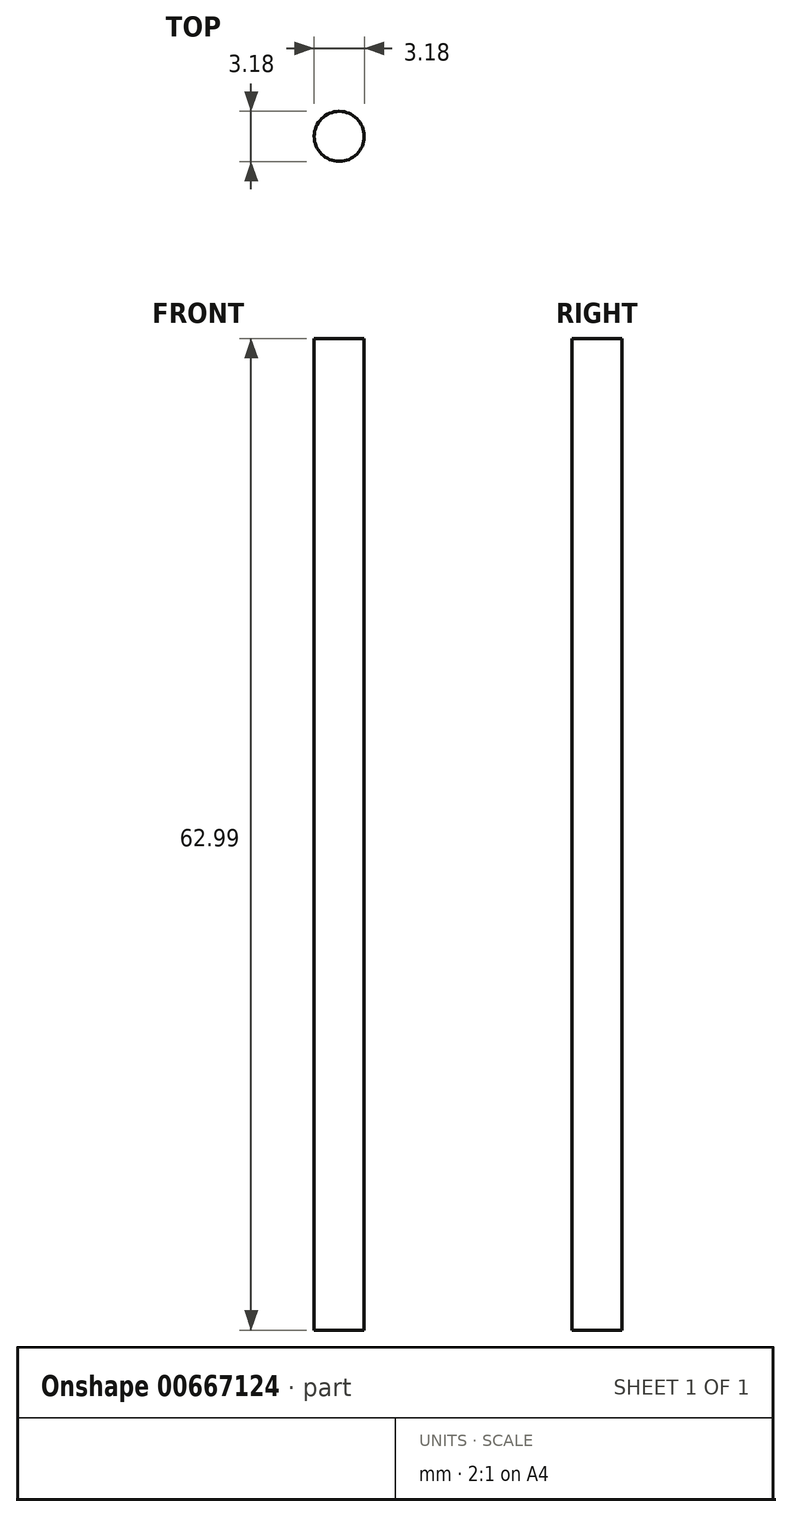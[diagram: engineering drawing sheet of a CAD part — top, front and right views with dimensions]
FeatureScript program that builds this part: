
annotation { "Feature Type Name" : "Feature", "Feature Type Description" : "" }
export const myFeature = defineFeature(function(context is Context, id is Id, definition is map)
    precondition{}
    {
        {
            var Q0;
            Q0=qCreatedBy(makeId("Top.planeOp"),FACE);
            var sketch = newSketch(context, id + "F0", { "sketchPlane" : qUnion([Q0])});
            skCircle(sketch, "E0", {"center": v(0, 0) * mm, "radius": 1.59 * mm});
            skSolve(sketch);
        }
        {
            var Q0;
            Q0 = qSketchRegion(id + "F0", true);
            extrude(context, id + "F1", {"entities" : qUnion([Q0]), "depth" : 63 * mm, "offsetDistance" : 25.4 * mm});
        }
    });
